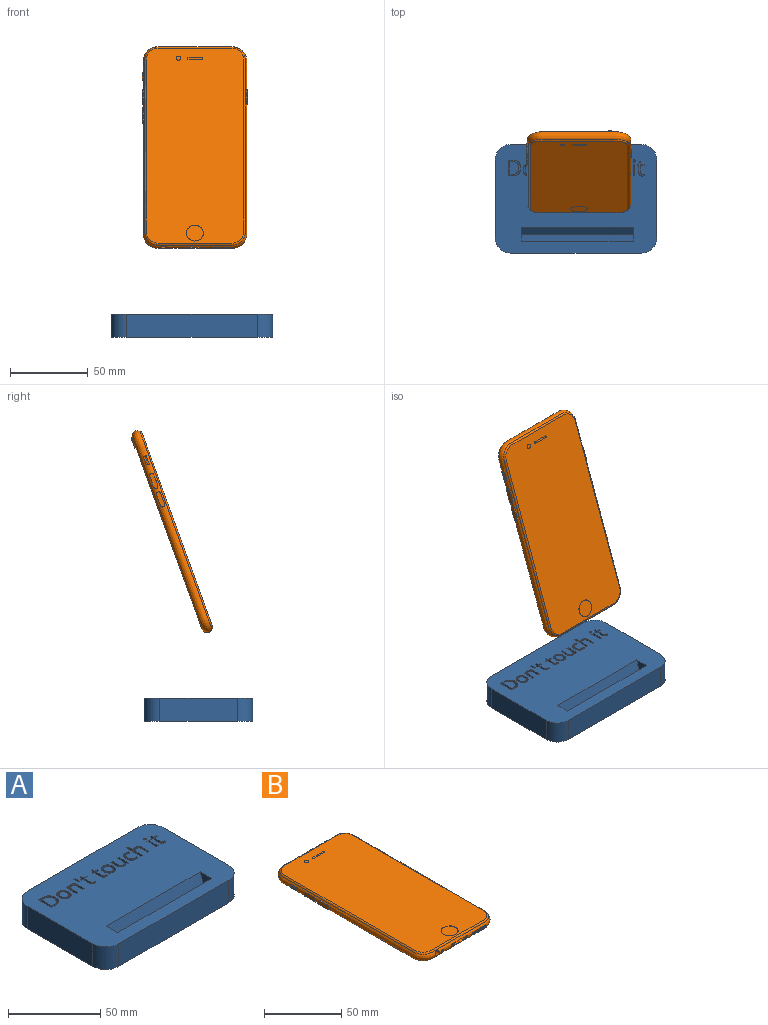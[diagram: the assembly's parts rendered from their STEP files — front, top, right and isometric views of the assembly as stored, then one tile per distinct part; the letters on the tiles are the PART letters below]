
ASSEMBLY  parts=2 mates=1
PART A: 219 faces, bbox 104.3x70x15 mm
  f0: plane 104.26x70mm, normal (0,0,1), area 6274.4mm2, adj f1,f2,f3,f4,f5,f6,f7,f8
  f1: plane 50x15mm, normal (-1,0,0), area 750mm2, adj f0,f2,f8,f9
  f2: cylinder r=10mm len=15mm, axis (0,0,-1), area 235.6mm2, adj f0,f1,f3,f9
  f3: plane 84.26x15mm, normal (0,-1,0), area 1263.9mm2, adj f0,f2,f4,f9
  f4: cylinder r=10mm len=15mm, axis (0,0,-1), area 235.6mm2, adj f0,f3,f5,f9
  f5: plane 50x15mm, normal (1,0,0), area 750mm2, adj f0,f4,f6,f9
  f6: cylinder r=10mm len=15mm, axis (0,0,-1), area 235.6mm2, adj f0,f5,f7,f9
  f7: plane 84.26x15mm, normal (0,1,0), area 1263.9mm2, adj f0,f6,f8,f9
  f8: cylinder r=10mm len=15mm, axis (0,0,-1), area 235.6mm2, adj f0,f1,f7,f9
  f9: plane 104.26x70mm, normal (0,0,-1), area 7212.5mm2, adj f1,f2,f3,f4,f5,f6,f7,f8
  f10: plane 72x13mm, normal (0,0.94,-0.34), area 996.1mm2, adj f0,f11,f13,f14
  f11: plane 72x8.83mm, normal (0,0,1), area 636mm2, adj f10,f12,f13,f14
  f12: plane 72x13mm, normal (0,-0.94,0.34), area 996.1mm2, adj f0,f11,f13,f14
  f13: plane 13.56x13mm, normal (1,0,0), area 114.8mm2, adj f0,f10,f11,f12
  f14: plane 13.56x13mm, normal (-1,0,0), area 114.8mm2, adj f0,f10,f11,f12
  f15: plane 4.91x2mm, normal (1,0,0), area 9.8mm2, adj f0,f16,f31,f32
  f16: plane 2x1.15mm, normal (0,1,0), area 2.3mm2, adj f0,f15,f17,f32
  f17: plane 4.95x2mm, normal (-1,0,0), area 9.9mm2, adj f0,f16,f18,f32
  f18: extruded ~2.12x2mm, area 4.6mm2, adj f0,f17,f19,f32
  f19: extruded ~2.06x2mm, area 4.4mm2, adj f0,f18,f20,f32
  f20: extruded ~2x1.42mm, area 2.9mm2, adj f0,f19,f21,f32
  f21: extruded ~2x0.99mm, area 2.7mm2, adj f0,f20,f22,f32
  f22: plane 2x0.06mm, normal (0,-1,0), area 0.1mm2, adj f0,f21,f23,f32
  f23: plane 2x1.04mm, normal (-0.98,-0.18,0), area 2.1mm2, adj f0,f22,f24,f32
  f24: plane 2x0.93mm, normal (0,-1,0), area 1.9mm2, adj f0,f23,f25,f32
  f25: plane 7.58x2mm, normal (1,0,0), area 15.2mm2, adj f0,f24,f26,f32
  f26: plane 2x1.15mm, normal (0,1,0), area 2.3mm2, adj f0,f25,f27,f32
  f27: plane 3.98x2mm, normal (-1,0,0), area 8mm2, adj f0,f26,f28,f32
  f28: extruded ~2.12x2mm, area 4.5mm2, adj f0,f27,f29,f32
  f29: extruded ~2x1.74mm, area 3.8mm2, adj f0,f28,f30,f32
  f30: extruded ~2x1.32mm, area 2.9mm2, adj f0,f29,f31,f32
  f31: extruded ~2x1.38mm, area 3mm2, adj f0,f15,f30,f32
  f32: plane 7.72x6.34mm, normal (0,0,1), area 20.8mm2, adj f15,f16,f17,f18,f19,f20,f21,f22
  f33: extruded ~2x0.59mm, area 1.2mm2, adj f0,f34,f51,f52
  f34: extruded ~2x0.89mm, area 2mm2, adj f0,f33,f35,f52
  f35: extruded ~2x1.05mm, area 2.2mm2, adj f0,f34,f36,f52
  f36: plane 4.46x2mm, normal (-1,0,0), area 8.9mm2, adj f0,f35,f37,f52
  f37: plane 2.2x2mm, normal (0,1,0), area 4.4mm2, adj f0,f36,f38,f52
  f38: plane 2x0.89mm, normal (-1,0,0), area 1.8mm2, adj f0,f37,f39,f52
  f39: plane 2.2x2mm, normal (0,-1,0), area 4.4mm2, adj f0,f38,f40,f52
  f40: plane 2x1.76mm, normal (-1,0,0), area 3.5mm2, adj f0,f39,f41,f52
  f41: plane 2x0.66mm, normal (0,-1,0), area 1.3mm2, adj f0,f40,f42,f52
  f42: plane 2x1.62mm, normal (0.96,-0.29,0), area 3.4mm2, adj f0,f41,f43,f52
  f43: plane 2x1.09mm, normal (0.4,-0.92,0), area 2.4mm2, adj f0,f42,f44,f52
  f44: plane 2x0.55mm, normal (1,0,0), area 1.1mm2, adj f0,f43,f45,f52
  f45: plane 2x1.09mm, normal (0,1,0), area 2.2mm2, adj f0,f44,f46,f52
  f46: plane 4.51x2mm, normal (1,0,0), area 9mm2, adj f0,f45,f47,f52
  f47: extruded ~2.32x2.2mm, area 7.3mm2, adj f0,f46,f48,f52
  f48: extruded ~2x0.66mm, area 1.3mm2, adj f0,f47,f49,f52
  f49: extruded ~2x0.55mm, area 1.1mm2, adj f0,f48,f50,f52
  f50: plane 2x0.88mm, normal (-1,0,0), area 1.8mm2, adj f0,f49,f51,f52
  f51: extruded ~2x0.45mm, area 0.9mm2, adj f0,f33,f50,f52
  f52: plane 9.48x4.49mm, normal (0,0,1), area 14.9mm2, adj f33,f34,f35,f36,f37,f38,f39,f40
  f53: extruded ~2.98x2mm, area 6.5mm2, adj f54,f66,f67,f216
  f54: extruded ~3.06x2mm, area 6.7mm2, adj f53,f55,f67,f216
  f55: extruded ~3.16x2mm, area 6.8mm2, adj f54,f56,f67,f216
  f56: plane 2x1.43mm, normal (0,-1,0), area 2.9mm2, adj f55,f57,f67,f216
  f57: plane 8.08x2mm, normal (-1,0,0), area 16.2mm2, adj f56,f58,f67,f216
  f58: plane 2x1.71mm, normal (0,1,0), area 3.4mm2, adj f57,f66,f67,f216
  f59: extruded ~3.83x2mm, area 8.4mm2, adj f0,f60,f65,f67
  f60: extruded ~3.65x2mm, area 8mm2, adj f0,f59,f61,f67
  f61: extruded ~3.67x2mm, area 8mm2, adj f0,f60,f62,f67
  f62: plane 3.1x2mm, normal (0,-1,0), area 6.2mm2, adj f0,f61,f63,f67
  f63: plane 10.12x2mm, normal (1,0,0), area 20.2mm2, adj f0,f62,f64,f67
  f64: plane 2.8x2mm, normal (0,1,0), area 5.6mm2, adj f0,f63,f65,f67
  f65: extruded ~3.91x2mm, area 8.5mm2, adj f0,f59,f64,f67
  f66: extruded ~2.95x2mm, area 6.4mm2, adj f53,f58,f67,f216
  f67: plane 10.12x8.08mm, normal (0,0,1), area 32.4mm2, adj f53,f54,f55,f56,f57,f58,f59,f60
  f68: extruded ~2.22x2mm, area 4.7mm2, adj f69,f84,f85,f217
  f69: extruded ~2.21x2mm, area 4.6mm2, adj f68,f70,f85,f217
  f70: extruded ~2x1.7mm, area 3.9mm2, adj f69,f71,f85,f217
  f71: extruded ~2x1.73mm, area 3.9mm2, adj f70,f72,f85,f217
  f72: extruded ~2.2x2mm, area 4.6mm2, adj f71,f73,f85,f217
  f73: extruded ~2.22x2mm, area 4.7mm2, adj f72,f74,f85,f217
  f74: extruded ~2x1.71mm, area 3.9mm2, adj f73,f84,f85,f217
  f75: extruded ~2.9x2mm, area 6.2mm2, adj f0,f76,f83,f85
  f76: extruded ~2.86x2mm, area 6.2mm2, adj f0,f75,f77,f85
  f77: extruded ~2.53x2mm, area 5.7mm2, adj f0,f76,f78,f85
  f78: extruded ~2.58x2mm, area 5.7mm2, adj f0,f77,f79,f85
  f79: extruded ~2.89x2mm, area 6.2mm2, adj f0,f78,f80,f85
  f80: extruded ~2.09x2mm, area 4.3mm2, adj f0,f79,f81,f85
  f81: extruded ~2x1.37mm, area 3.7mm2, adj f0,f80,f82,f85
  f82: extruded ~2x1.81mm, area 3.8mm2, adj f0,f81,f83,f85
  f83: extruded ~2.58x2mm, area 5.7mm2, adj f0,f75,f82,f85
  f84: extruded ~2x1.71mm, area 3.9mm2, adj f68,f74,f85,f217
  f85: plane 7.86x6.97mm, normal (0,0,1), area 22.1mm2, adj f68,f69,f70,f71,f72,f73,f74,f75
  f86: extruded ~2.22x2mm, area 4.7mm2, adj f87,f102,f103,f218
  f87: extruded ~2.21x2mm, area 4.6mm2, adj f86,f88,f103,f218
  f88: extruded ~2x1.7mm, area 3.9mm2, adj f87,f89,f103,f218
  f89: extruded ~2x1.73mm, area 3.9mm2, adj f88,f90,f103,f218
  f90: extruded ~2.2x2mm, area 4.6mm2, adj f89,f91,f103,f218
  f91: extruded ~2.22x2mm, area 4.7mm2, adj f90,f92,f103,f218
  f92: extruded ~2x1.71mm, area 3.9mm2, adj f91,f102,f103,f218
  f93: extruded ~2.9x2mm, area 6.2mm2, adj f0,f94,f101,f103
  f94: extruded ~2.86x2mm, area 6.2mm2, adj f0,f93,f95,f103
  f95: extruded ~2.53x2mm, area 5.7mm2, adj f0,f94,f96,f103
  f96: extruded ~2.58x2mm, area 5.7mm2, adj f0,f95,f97,f103
  f97: extruded ~2.89x2mm, area 6.2mm2, adj f0,f96,f98,f103
  f98: extruded ~2.09x2mm, area 4.3mm2, adj f0,f97,f99,f103
  f99: extruded ~2x1.37mm, area 3.7mm2, adj f0,f98,f100,f103
  f100: extruded ~2x1.81mm, area 3.8mm2, adj f0,f99,f101,f103
  f101: extruded ~2.58x2mm, area 5.7mm2, adj f0,f93,f100,f103
  f102: extruded ~2x1.71mm, area 3.9mm2, adj f86,f92,f103,f218
  f103: plane 7.86x6.97mm, normal (0,0,1), area 22.1mm2, adj f86,f87,f88,f89,f90,f91,f92,f93
  f104: extruded ~2x0.58mm, area 1.3mm2, adj f0,f105,f111,f112
  f105: extruded ~2x0.58mm, area 1.3mm2, adj f0,f104,f106,f112
  f106: extruded ~2x0.49mm, area 1.1mm2, adj f0,f105,f107,f112
  f107: extruded ~2x0.48mm, area 1.1mm2, adj f0,f106,f108,f112
  f108: extruded ~2x0.58mm, area 1.3mm2, adj f0,f107,f109,f112
  f109: extruded ~2x0.57mm, area 1.3mm2, adj f0,f108,f110,f112
  f110: extruded ~2x0.48mm, area 1.1mm2, adj f0,f109,f111,f112
  f111: extruded ~2x0.49mm, area 1.1mm2, adj f0,f104,f110,f112
  f112: plane 1.53x1.36mm, normal (0,0,1), area 1.7mm2, adj f104,f105,f106,f107,f108,f109,f110,f111
  f113: plane 2x1.15mm, normal (0,1,0), area 2.3mm2, adj f0,f114,f116,f117
  f114: plane 7.58x2mm, normal (-1,0,0), area 15.2mm2, adj f0,f113,f115,f117
  f115: plane 2x1.15mm, normal (0,-1,0), area 2.3mm2, adj f0,f114,f116,f117
  f116: plane 7.58x2mm, normal (1,0,0), area 15.2mm2, adj f0,f113,f115,f117
  f117: plane 7.58x1.15mm, normal (0,0,1), area 8.7mm2, adj f113,f114,f115,f116
  f118: plane 4.91x2mm, normal (1,0,0), area 9.8mm2, adj f0,f119,f135,f136
  f119: plane 2x1.15mm, normal (0,1,0), area 2.3mm2, adj f0,f118,f120,f136
  f120: plane 4.95x2mm, normal (-1,0,0), area 9.9mm2, adj f0,f119,f121,f136
  f121: extruded ~2.1x2mm, area 4.5mm2, adj f0,f120,f122,f136
  f122: extruded ~2.09x2mm, area 4.5mm2, adj f0,f121,f123,f136
  f123: extruded ~2x1.43mm, area 3mm2, adj f0,f122,f124,f136
  f124: extruded ~2x0.97mm, area 2.6mm2, adj f0,f123,f125,f136
  f125: plane 2x0.07mm, normal (0,-1,0), area 0.1mm2, adj f0,f124,f126,f136
  f126: extruded ~2x0.98mm, area 2mm2, adj f0,f125,f127,f136
  f127: plane 3.26x2mm, normal (-1,0,0), area 6.5mm2, adj f0,f126,f128,f136
  f128: plane 2x1.15mm, normal (0,-1,0), area 2.3mm2, adj f0,f127,f129,f136
  f129: plane 10.77x2mm, normal (1,0,0), area 21.5mm2, adj f0,f128,f130,f136
  f130: plane 2x1.15mm, normal (0,1,0), area 2.3mm2, adj f0,f129,f131,f136
  f131: plane 3.97x2mm, normal (-1,0,0), area 7.9mm2, adj f0,f130,f132,f136
  f132: extruded ~2.13x2mm, area 4.5mm2, adj f0,f131,f133,f136
  f133: extruded ~2x1.75mm, area 3.9mm2, adj f0,f132,f134,f136
  f134: extruded ~2x1.32mm, area 2.9mm2, adj f0,f133,f135,f136
  f135: extruded ~2x1.38mm, area 3mm2, adj f0,f118,f134,f136
  f136: plane 10.77x6.34mm, normal (0,0,1), area 24.6mm2, adj f118,f119,f120,f121,f122,f123,f124,f125
  f137: extruded ~2.55x2mm, area 5.7mm2, adj f0,f138,f151,f152
  f138: extruded ~2x1.92mm, area 3.9mm2, adj f0,f137,f139,f152
  f139: plane 2x1.02mm, normal (-1,0,0), area 2mm2, adj f0,f138,f140,f152
  f140: extruded ~2x1.94mm, area 4mm2, adj f0,f139,f141,f152
  f141: extruded ~2x1.67mm, area 3.8mm2, adj f0,f140,f142,f152
  f142: extruded ~2.14x2mm, area 4.5mm2, adj f0,f141,f143,f152
  f143: extruded ~2.95x2.31mm, area 8.6mm2, adj f0,f142,f144,f152
  f144: extruded ~2x0.8mm, area 1.6mm2, adj f0,f143,f145,f152
  f145: extruded ~2x0.83mm, area 1.7mm2, adj f0,f144,f146,f152
  f146: plane 2x0.97mm, normal (-0.94,0.34,0), area 2.1mm2, adj f0,f145,f147,f152
  f147: extruded ~2x0.86mm, area 1.8mm2, adj f0,f146,f148,f152
  f148: extruded ~2x1.09mm, area 2.2mm2, adj f0,f147,f149,f152
  f149: extruded ~2.61x2mm, area 5.8mm2, adj f0,f148,f150,f152
  f150: extruded ~2.94x2mm, area 6.3mm2, adj f0,f149,f151,f152
  f151: extruded ~2.87x2mm, area 6.2mm2, adj f0,f137,f150,f152
  f152: plane 7.86x5.48mm, normal (0,0,1), area 15.3mm2, adj f137,f138,f139,f140,f141,f142,f143,f144
  f153: plane 4.92x2mm, normal (-1,0,0), area 9.8mm2, adj f0,f154,f169,f170
  f154: plane 2x1.16mm, normal (0,-1,0), area 2.3mm2, adj f0,f153,f155,f170
  f155: plane 4.96x2mm, normal (1,0,0), area 9.9mm2, adj f0,f154,f156,f170
  f156: extruded ~2.1x2mm, area 4.5mm2, adj f0,f155,f157,f170
  f157: extruded ~2.07x2mm, area 4.5mm2, adj f0,f156,f158,f170
  f158: extruded ~2x1.43mm, area 2.9mm2, adj f0,f157,f159,f170
  f159: extruded ~2x0.98mm, area 2.6mm2, adj f0,f158,f160,f170
  f160: plane 2x0.06mm, normal (0,1,0), area 0.1mm2, adj f0,f159,f161,f170
  f161: plane 2x1.02mm, normal (0.99,0.16,0), area 2.1mm2, adj f0,f160,f162,f170
  f162: plane 2x0.95mm, normal (0,1,0), area 1.9mm2, adj f0,f161,f163,f170
  f163: plane 7.58x2mm, normal (-1,0,0), area 15.2mm2, adj f0,f162,f164,f170
  f164: plane 2x1.15mm, normal (0,-1,0), area 2.3mm2, adj f0,f163,f165,f170
  f165: plane 3.99x2mm, normal (1,0,0), area 8mm2, adj f0,f164,f166,f170
  f166: extruded ~2.12x2mm, area 4.5mm2, adj f0,f165,f167,f170
  f167: extruded ~2x1.74mm, area 3.8mm2, adj f0,f166,f168,f170
  f168: extruded ~2x1.32mm, area 2.9mm2, adj f0,f167,f169,f170
  f169: extruded ~2x1.38mm, area 3mm2, adj f0,f153,f168,f170
  f170: plane 7.72x6.34mm, normal (0,0,1), area 20.9mm2, adj f153,f154,f155,f156,f157,f158,f159,f160
  f171: extruded ~2x0.59mm, area 1.2mm2, adj f0,f172,f189,f190
  f172: extruded ~2x0.89mm, area 2mm2, adj f0,f171,f173,f190
  f173: extruded ~2x1.05mm, area 2.2mm2, adj f0,f172,f174,f190
  f174: plane 4.46x2mm, normal (-1,0,0), area 8.9mm2, adj f0,f173,f175,f190
  f175: plane 2.2x2mm, normal (0,1,0), area 4.4mm2, adj f0,f174,f176,f190
  f176: plane 2x0.89mm, normal (-1,0,0), area 1.8mm2, adj f0,f175,f177,f190
  f177: plane 2.2x2mm, normal (0,-1,0), area 4.4mm2, adj f0,f176,f178,f190
  f178: plane 2x1.76mm, normal (-1,0,0), area 3.5mm2, adj f0,f177,f179,f190
  f179: plane 2x0.66mm, normal (0,-1,0), area 1.3mm2, adj f0,f178,f180,f190
  f180: plane 2x1.62mm, normal (0.96,-0.29,0), area 3.4mm2, adj f0,f179,f181,f190
  f181: plane 2x1.09mm, normal (0.4,-0.92,0), area 2.4mm2, adj f0,f180,f182,f190
  f182: plane 2x0.55mm, normal (1,0,0), area 1.1mm2, adj f0,f181,f183,f190
  f183: plane 2x1.09mm, normal (0,1,0), area 2.2mm2, adj f0,f182,f184,f190
  f184: plane 4.51x2mm, normal (1,0,0), area 9mm2, adj f0,f183,f185,f190
  f185: extruded ~2.32x2.2mm, area 7.3mm2, adj f0,f184,f186,f190
  f186: extruded ~2x0.66mm, area 1.3mm2, adj f0,f185,f187,f190
  f187: extruded ~2x0.55mm, area 1.1mm2, adj f0,f186,f188,f190
  f188: plane 2x0.88mm, normal (-1,0,0), area 1.8mm2, adj f0,f187,f189,f190
  f189: extruded ~2x0.45mm, area 0.9mm2, adj f0,f171,f188,f190
  f190: plane 9.48x4.49mm, normal (0,0,1), area 14.9mm2, adj f171,f172,f173,f174,f175,f176,f177,f178
  f191: extruded ~2x0.59mm, area 1.2mm2, adj f0,f192,f209,f210
  f192: extruded ~2x0.89mm, area 2mm2, adj f0,f191,f193,f210
  f193: extruded ~2x1.05mm, area 2.2mm2, adj f0,f192,f194,f210
  f194: plane 4.46x2mm, normal (-1,0,0), area 8.9mm2, adj f0,f193,f195,f210
  f195: plane 2.2x2mm, normal (0,1,0), area 4.4mm2, adj f0,f194,f196,f210
  f196: plane 2x0.89mm, normal (-1,0,0), area 1.8mm2, adj f0,f195,f197,f210
  f197: plane 2.2x2mm, normal (0,-1,0), area 4.4mm2, adj f0,f196,f198,f210
  f198: plane 2x1.76mm, normal (-1,0,0), area 3.5mm2, adj f0,f197,f199,f210
  f199: plane 2x0.66mm, normal (0,-1,0), area 1.3mm2, adj f0,f198,f200,f210
  f200: plane 2x1.62mm, normal (0.96,-0.29,0), area 3.4mm2, adj f0,f199,f201,f210
  f201: plane 2x1.09mm, normal (0.4,-0.92,0), area 2.4mm2, adj f0,f200,f202,f210
  f202: plane 2x0.55mm, normal (1,0,0), area 1.1mm2, adj f0,f201,f203,f210
  f203: plane 2x1.09mm, normal (0,1,0), area 2.2mm2, adj f0,f202,f204,f210
  f204: plane 4.51x2mm, normal (1,0,0), area 9mm2, adj f0,f203,f205,f210
  f205: extruded ~2.32x2.2mm, area 7.3mm2, adj f0,f204,f206,f210
  f206: extruded ~2x0.66mm, area 1.3mm2, adj f0,f205,f207,f210
  f207: extruded ~2x0.55mm, area 1.1mm2, adj f0,f206,f208,f210
  f208: plane 2x0.88mm, normal (-1,0,0), area 1.8mm2, adj f0,f207,f209,f210
  f209: extruded ~2x0.45mm, area 0.9mm2, adj f0,f191,f208,f210
  f210: plane 9.48x4.49mm, normal (0,0,1), area 14.9mm2, adj f191,f192,f193,f194,f195,f196,f197,f198
  f211: plane 3.65x2mm, normal (-1,0.08,0), area 7.3mm2, adj f0,f212,f214,f215
  f212: plane 2x1.29mm, normal (0,-1,0), area 2.6mm2, adj f0,f211,f213,f215
  f213: plane 3.65x2mm, normal (1,0.08,0), area 7.3mm2, adj f0,f212,f214,f215
  f214: plane 2x0.73mm, normal (0,1,0), area 1.5mm2, adj f0,f211,f213,f215
  f215: plane 3.65x1.29mm, normal (0,0,1), area 3.7mm2, adj f211,f212,f213,f214
  f216: plane 8.08x5.66mm, normal (0,0,1), area 40.1mm2, adj f53,f54,f55,f56,f57,f58,f66
  f217: plane 5.92x4.59mm, normal (0,0,1), area 22.5mm2, adj f68,f69,f70,f71,f72,f73,f74,f84
  f218: plane 5.92x4.59mm, normal (0,0,1), area 22.5mm2, adj f86,f87,f88,f89,f90,f91,f92,f102
PART B: 76 faces, bbox 67.9x138.3x7.9 mm
  f0: cylinder r=0.8mm len=1.6mm, axis (0,1,0), area 1mm2, adj f18,f75
  f1: cylinder r=0.8mm len=1.6mm, axis (0,1,0), area 1mm2, adj f18,f74
  f2: cylinder r=0.8mm len=1.6mm, axis (0,-1,0), area 0.9mm2, adj f18,f73
  f3: cylinder r=0.8mm len=1.6mm, axis (0,-1,0), area 1mm2, adj f18,f72
  f4: cylinder r=0.8mm len=1.6mm, axis (0,-1,0), area 1mm2, adj f18,f71
  f5: cylinder r=0.8mm len=1.6mm, axis (0,-1,0), area 1mm2, adj f18,f70
  f6: cylinder r=0.8mm len=1.6mm, axis (0,-1,0), area 1mm2, adj f18,f69
  f7: cylinder r=0.8mm len=1.6mm, axis (0,-1,0), area 1mm2, adj f18,f68
  f8: cylinder r=0.8mm len=1.6mm, axis (0,-1,0), area 1mm2, adj f18,f67
  f9: cylinder r=2.02mm len=14.4mm, axis (0,1,0), area 182mm2, adj f18,f66
  f10: cylinder r=0.56mm len=1.11mm, axis (-1,0,0), area 0.7mm2, adj f18,f60
  f11: cylinder r=5.45mm len=10.9mm, axis (0,0,1), area 8.6mm2, adj f20,f30
  f12: cylinder r=1.43mm len=2.85mm, axis (0,0,1), area 0.1mm2, adj f20,f29
  f13: cylinder r=0.6mm len=1.2mm, axis (0,0,1), area 0.2mm2, adj f20,f26,f27,f28
  f14: cylinder r=2.06mm len=4.11mm, axis (0,0,-1), area 1.3mm2, adj f21,f24
  f15: cylinder r=0.75mm len=1.5mm, axis (0,0,-1), area 0.5mm2, adj f21,f23
  f16: cylinder r=3.6mm len=7.2mm, axis (0,0,1), area 17.4mm2, adj f21,f22
  f17: bspline ~135.99x64.82mm, area 589.2mm2, adj f18,f20
  f18: bspline ~138.14x66.97mm, area 2894.6mm2, adj f0,f1,f2,f3,f4,f5,f6,f7
  f19: plane 1.02x0.41mm, normal (0,1,0), area 0.3mm2, adj f18,f31,f35,f36
  f20: plane 134.1x62.93mm, normal (0,0,1), area 8237.3mm2, adj f11,f12,f13,f17,f25,f26,f27
  f21: plane 132x60.83mm, normal (0,0,-1), area 7934.9mm2, adj f14,f15,f16,f18
  f22: plane 7.2x7.2mm, normal (0,0,-1), area 40.7mm2, adj f16
  f23: plane 1.5x1.5mm, normal (0,0,-1), area 1.8mm2, adj f15
  f24: plane 4.11x4.11mm, normal (0,0,-1), area 13.3mm2, adj f14
  f25: cylinder r=0.6mm len=1.2mm, axis (0,0,1), area 0.2mm2, adj f20,f26,f27,f28
  f26: plane 9x0.1mm, normal (0,-1,0), area 0.9mm2, adj f13,f20,f25,f28
  f27: plane 9x0.1mm, normal (0,1,0), area 0.9mm2, adj f13,f20,f25,f28
  f28: plane 10.2x1.2mm, normal (0,0,1), area 11.9mm2, adj f13,f25,f26,f27
  f29: plane 2.85x2.85mm, normal (0,0,1), area 6.4mm2, adj f12
  f30: plane 10.9x10.9mm, normal (0,0,1), area 93.3mm2, adj f11
  f31: cylinder r=0.25mm len=0.28mm, axis (1,0,0), area 0.1mm2, adj f18,f19,f32,f35
  f32: plane 5.12x0.21mm, normal (0,0,-1), area 1mm2, adj f18,f31,f33,f35
  f33: cylinder r=0.25mm len=0.27mm, axis (1,0,0), area 0.1mm2, adj f18,f32,f34,f35
  f34: plane 1.01x0.41mm, normal (0,-1,0), area 0.3mm2, adj f18,f33,f35,f38
  f35: plane 5.61x1.24mm, normal (-1,0,0), area 5.6mm2, adj f19,f31,f32,f33,f34,f36,f37,f38
  f36: cylinder r=0.25mm len=0.81mm, axis (1,0,0), area 0.3mm2, adj f19,f35,f37,f43,f44
  f37: plane 5.11x0.81mm, normal (0,0,1), area 4.1mm2, adj f35,f36,f38,f44
  f38: cylinder r=0.25mm len=0.81mm, axis (1,0,0), area 0.3mm2, adj f34,f35,f37,f39,f44
  f39: plane 0.51x0.49mm, normal (0,1,0), area 0.2mm2, adj f18,f38,f40,f44
  f40: cylinder r=0.25mm len=0.57mm, axis (1,0,0), area 0.2mm2, adj f18,f39,f41,f44
  f41: plane 5.12x0.58mm, normal (0,0,-1), area 2.9mm2, adj f18,f40,f42,f44
  f42: cylinder r=0.25mm len=0.57mm, axis (1,0,0), area 0.2mm2, adj f18,f41,f43,f44
  f43: plane 0.51x0.5mm, normal (0,-1,0), area 0.2mm2, adj f18,f36,f42,f44
  f44: plane 5.61x0.99mm, normal (-1,0,0), area 5.5mm2, adj f36,f37,f38,f39,f40,f41,f42,f43
  f45: plane 7.41x0.64mm, normal (0,0,1), area 4.6mm2, adj f18,f46,f48,f49
  f46: cylinder r=1.4mm len=2.8mm, axis (1,0,0), area 2mm2, adj f18,f45,f47,f49
  f47: plane 7.4x0.6mm, normal (0,0,-1), area 4.4mm2, adj f18,f46,f48,f49
  f48: cylinder r=1.4mm len=2.8mm, axis (1,0,0), area 2mm2, adj f18,f45,f47,f49
  f49: plane 10.2x2.8mm, normal (-1,0,0), area 26.9mm2, adj f45,f46,f47,f48
  f50: plane 7.4x0.62mm, normal (0,0,1), area 4.5mm2, adj f18,f51,f53,f54
  f51: cylinder r=1.4mm len=2.8mm, axis (1,0,0), area 2mm2, adj f18,f50,f52,f54
  f52: plane 7.4x0.59mm, normal (0,0,-1), area 4.4mm2, adj f18,f51,f53,f54
  f53: cylinder r=1.4mm len=2.8mm, axis (1,0,0), area 2mm2, adj f18,f50,f52,f54
  f54: plane 10.2x2.8mm, normal (-1,0,0), area 26.9mm2, adj f50,f51,f52,f53
  f55: cylinder r=1.4mm len=2.8mm, axis (-1,0,0), area 2mm2, adj f18,f56,f58,f59
  f56: plane 7.41x0.64mm, normal (0,0,1), area 4.6mm2, adj f18,f55,f57,f59
  f57: cylinder r=1.4mm len=2.8mm, axis (-1,0,0), area 2mm2, adj f18,f56,f58,f59
  f58: plane 7.4x0.6mm, normal (0,0,-1), area 4.4mm2, adj f18,f55,f57,f59
  f59: plane 10.2x2.8mm, normal (1,0,0), area 26.9mm2, adj f55,f56,f57,f58
  f60: plane 1.11x1.11mm, normal (1,0,0), area 1mm2, adj f10
  f61: cylinder r=0.99mm len=6.47mm, axis (0,1,0), area 20.1mm2, adj f18,f62,f64,f65
  f62: plane 6.72x6.44mm, normal (0,0,1), area 43.3mm2, adj f18,f61,f63,f65
  f63: cylinder r=0.99mm len=6.47mm, axis (0,1,0), area 20.1mm2, adj f18,f62,f64,f65
  f64: plane 6.73x6.48mm, normal (0,0,-1), area 43.5mm2, adj f18,f61,f63,f65
  f65: plane 8.7x1.98mm, normal (0,-1,0), area 16.4mm2, adj f61,f62,f63,f64
  f66: plane 4.04x4.04mm, normal (0,-1,0), area 12.8mm2, adj f9
  f67: plane 1.6x1.6mm, normal (0,-1,0), area 2mm2, adj f8
  f68: plane 1.6x1.6mm, normal (0,-1,0), area 2mm2, adj f7
  f69: plane 1.6x1.6mm, normal (0,-1,0), area 2mm2, adj f6
  f70: plane 1.6x1.6mm, normal (0,-1,0), area 2mm2, adj f5
  f71: plane 1.6x1.6mm, normal (0,-1,0), area 2mm2, adj f4
  f72: plane 1.6x1.6mm, normal (0,-1,0), area 2mm2, adj f3
  f73: plane 1.6x1.6mm, normal (0,-1,0), area 2mm2, adj f2
  f74: plane 1.6x1.6mm, normal (0,-1,0), area 2mm2, adj f1
  f75: plane 1.6x1.6mm, normal (0,-1,0), area 2mm2, adj f0
PLACE A t=(2.14,2.15,-8.39)mm fixed
PLACE B rot(axis=(1,0,0),70deg) t=(3.2,27.37,114.09)mm
MATE planar B.f21 <-> A.f12  axis (0,0.94,-0.34) through (3.08,30.47,112.5)mm
